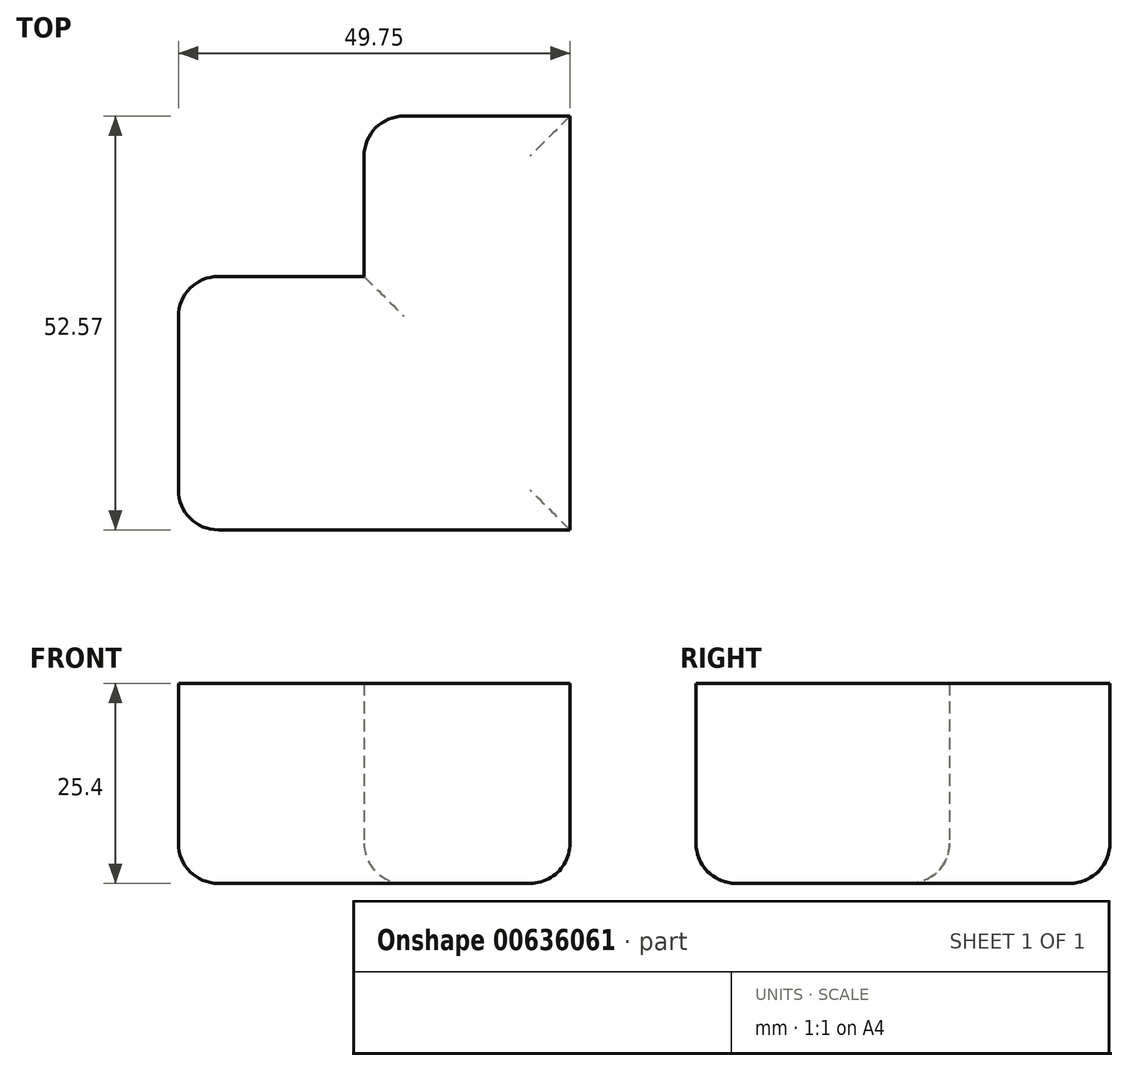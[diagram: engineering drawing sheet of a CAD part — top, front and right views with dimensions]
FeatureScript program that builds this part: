
annotation { "Feature Type Name" : "Feature", "Feature Type Description" : "" }
export const myFeature = defineFeature(function(context is Context, id is Id, definition is map)
    precondition{}
    {
        {
            var Q0;
            Q0=qCreatedBy(makeId("Top.planeOp"),FACE);
            var sketch = newSketch(context, id + "F0", { "sketchPlane" : qUnion([Q0])});
            skLineSegment(sketch, "E0.bottom", {"start": v(0, 0) * mm, "end": v(0, 0) * mm});
            skLineSegment(sketch, "E0.top", {"start": v(0, 0) * mm, "end": v(0, 0) * mm});
            skLineSegment(sketch, "E0.left", {"start": v(0, 0) * mm, "end": v(0, 0) * mm});
            skLineSegment(sketch, "E0.right", {"start": v(0, 0) * mm, "end": v(0, 0) * mm});
            skLineSegment(sketch, "E1.bottom", {"start": v(26.16, -14.62) * mm, "end": v(-23.59, -14.62) * mm});
            skLineSegment(sketch, "E1.top", {"start": v(26.16, 17.57) * mm, "end": v(-23.59, 17.57) * mm});
            skLineSegment(sketch, "E1.left", {"start": v(26.16, -14.62) * mm, "end": v(26.16, 17.57) * mm});
            skLineSegment(sketch, "E1.right", {"start": v(-23.59, -14.62) * mm, "end": v(-23.59, 17.57) * mm});
            skLineSegment(sketch, "E2.bottom", {"start": v(-23.59, 1.48) * mm, "end": v(26.16, 1.48) * mm});
            skLineSegment(sketch, "E2.top", {"start": v(-23.59, 1.48) * mm, "end": v(26.16, 1.48) * mm});
            skLineSegment(sketch, "E2.left", {"start": v(-23.59, 1.48) * mm, "end": v(-23.59, 1.48) * mm});
            skLineSegment(sketch, "E2.right", {"start": v(26.16, 1.48) * mm, "end": v(26.16, 1.48) * mm});
            skLineSegment(sketch, "E3.bottom", {"start": v(0, 37.95) * mm, "end": v(26.16, 37.95) * mm});
            skLineSegment(sketch, "E3.top", {"start": v(0, -14.62) * mm, "end": v(26.16, -14.62) * mm});
            skLineSegment(sketch, "E3.left", {"start": v(0, 37.95) * mm, "end": v(0, -14.62) * mm});
            skLineSegment(sketch, "E3.right", {"start": v(26.16, 37.95) * mm, "end": v(26.16, -14.62) * mm});
            skLineSegment(sketch, "E4.bottom", {"start": v(42.86, -46.58) * mm, "end": v(-27, -46.58) * mm});
            skLineSegment(sketch, "E4.top", {"start": v(42.86, -41.43) * mm, "end": v(-27, -41.43) * mm});
            skLineSegment(sketch, "E4.left", {"start": v(42.86, -46.58) * mm, "end": v(42.86, -41.43) * mm});
            skLineSegment(sketch, "E4.right", {"start": v(-27, -46.58) * mm, "end": v(-27, -41.43) * mm});
            skSolve(sketch);
        }
        {
            var Q0;
            {var subQ0=sQuery(id+"F0.wireOp",EDGE,"E1.bottom");Q0=makeQuery(id+"F0.imprint","IMPRINT",FACE,{"disambiguationData":[TD([[makeQuery(id+"F0.imprint","IMPRINT",EDGE,{"derivedFrom":subQ0}),-1.0]])]});}
            var Q1;
            {var subQ0=sQuery(id+"F0.wireOp",EDGE,"E3.right");var subQ1=sQuery(id+"F0.wireOp",EDGE,"E1.top");var subQ2=makeQuery(id+"F0.imprint","INTERSECT",VERTEX,{"derivedFrom":[subQ1,subQ0]});Q1=makeQuery(id+"F0.imprint","IMPRINT",FACE,{"disambiguationData":[TD([[makeQuery(id+"F0.imprint","IMPRINT",EDGE,{"disambiguationData":[TD([[subQ2,-1.0]])],"derivedFrom":subQ1}),1.0]])]});}
            var Q2;
            {var subQ0=sQuery(id+"F0.wireOp",EDGE,"E1.right");var subQ1=sQuery(id+"F0.wireOp",EDGE,"E1.top");var subQ2=makeQuery(id+"F0.imprint","INTERSECT",VERTEX,{"derivedFrom":[subQ1,subQ0]});Q2=makeQuery(id+"F0.imprint","IMPRINT",FACE,{"disambiguationData":[TD([[makeQuery(id+"F0.imprint","IMPRINT",EDGE,{"disambiguationData":[TD([[subQ2,1.0]])],"derivedFrom":subQ1}),1.0]])]});}
            var Q3;
            {var subQ5=sQuery(id+"F0.wireOp",EDGE,"E3.bottom");Q3=makeQuery(id+"F0.imprint","IMPRINT",FACE,{"disambiguationData":[TD([[makeQuery(id+"F0.imprint","IMPRINT",EDGE,{"derivedFrom":subQ5}),-1.0]])]});}
            var Q4;
            {var subQ5=sQuery(id+"F0.wireOp",EDGE,"E3.top");Q4=makeQuery(id+"F0.imprint","IMPRINT",FACE,{"disambiguationData":[TD([[makeQuery(id+"F0.imprint","IMPRINT",EDGE,{"derivedFrom":subQ5}),1.0]])]});}
            extrude(context, id + "F1", {"entities" : qUnion([Q0, Q1, Q2, Q3, Q4]), "depth" : 25.4 * mm, "offsetDistance" : 25.4 * mm});
        }
        {
            var Q0;
            Q0=makeQuery(id+"F1.opExtrude","CAP_EDGE",EDGE,{"disambiguationData":[OSD([sQuery(id+"F0.wireOp",EDGE,"E1.right")])],"isStart":true});
            fillet(context, id + "F2", {"entities" : qUnion([Q0]), "radius" : 5.08 * mm, "tangentPropagation" : true, "allowEdgeOverflow" : false});
        }
        {
            var Q0;
            Q0=makeQuery(id+"F1.opExtrude","CAP_FACE",FACE,{"disambiguationData":[OSD([sQuery(id+"F0.wireOp",EDGE,"E1.bottom"),sQuery(id+"F0.wireOp",EDGE,"E1.top"),sQuery(id+"F0.wireOp",EDGE,"E1.right"),sQuery(id+"F0.wireOp",EDGE,"E3.bottom"),sQuery(id+"F0.wireOp",EDGE,"E3.top"),sQuery(id+"F0.wireOp",EDGE,"E3.left"),sQuery(id+"F0.wireOp",EDGE,"E3.right")])],"isStart":true});
            fillet(context, id + "F3", {"entities" : qUnion([Q0]), "radius" : 5.08 * mm, "tangentPropagation" : true, "allowEdgeOverflow" : false});
        }
        {
            var Q0;
            Q0=makeQuery(id+"F3.opFillet","BLEND_EDGE",EDGE,{"blendedFrom":[makeQuery(id+"F1.opExtrude","CAP_EDGE",EDGE,{"disambiguationData":[OSD([sQuery(id+"F0.wireOp",EDGE,"E3.bottom")])],"isStart":true}),makeQuery(id+"F1.opExtrude","CAP_EDGE",EDGE,{"disambiguationData":[OSD([sQuery(id+"F0.wireOp",EDGE,"E3.left")])],"isStart":true})],"blendedInto":[]});
            fillet(context, id + "F4", {"entities" : qUnion([Q0]), "radius" : 5.08 * mm, "tangentPropagation" : true, "allowEdgeOverflow" : false});
        }
    });
